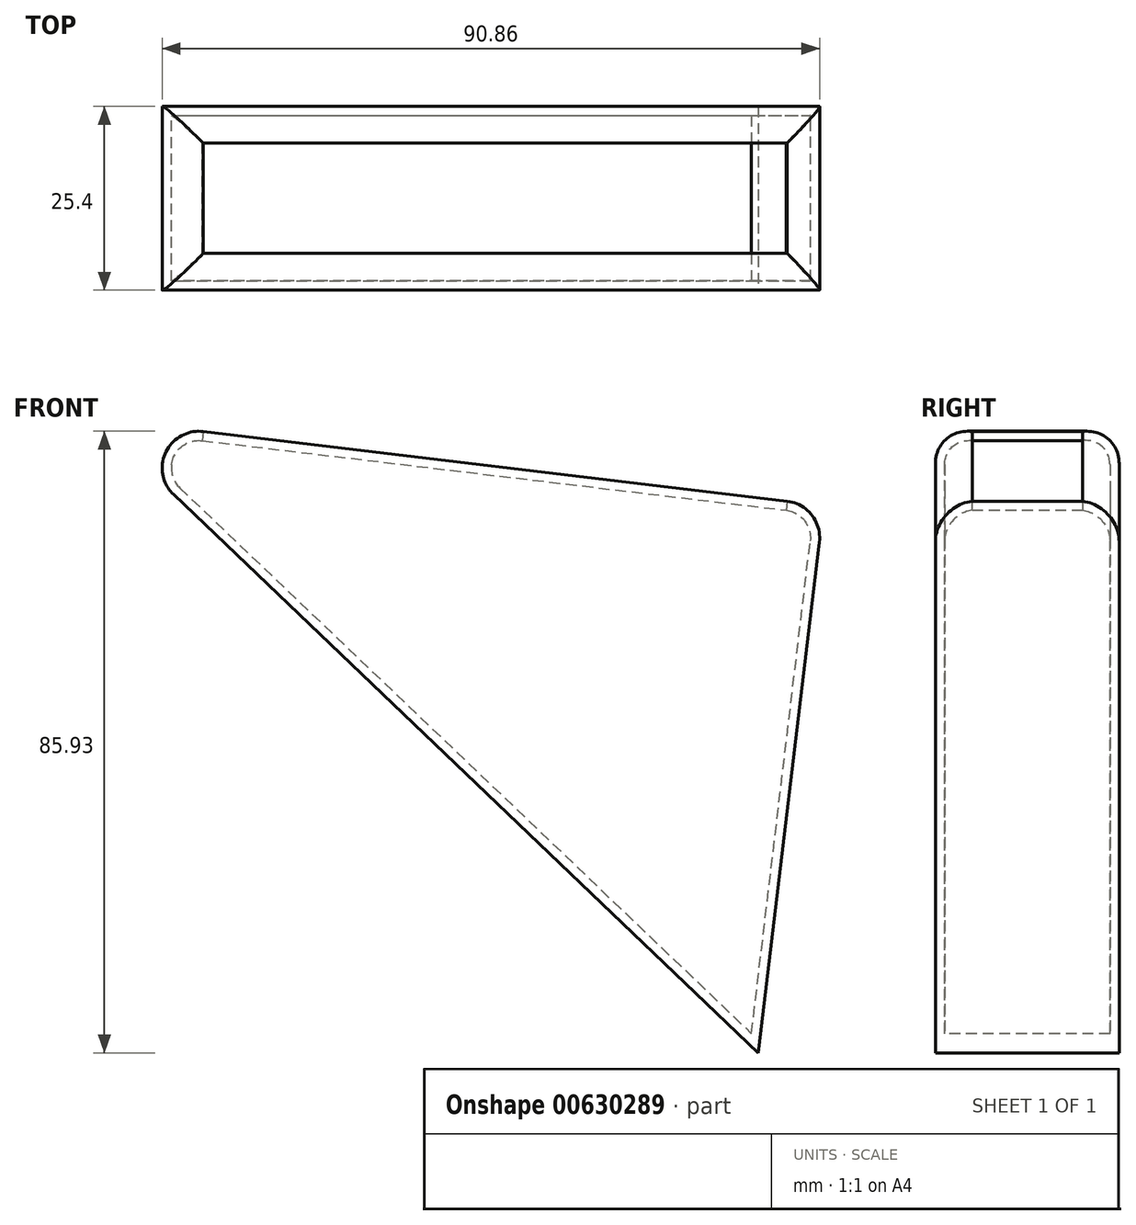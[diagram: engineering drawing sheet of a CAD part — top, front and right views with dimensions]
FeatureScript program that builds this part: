
annotation { "Feature Type Name" : "Feature", "Feature Type Description" : "" }
export const myFeature = defineFeature(function(context is Context, id is Id, definition is map)
    precondition{}
    {
        {
            var Q0;
            Q0=qCreatedBy(makeId("Front.planeOp"),FACE);
            var sketch = newSketch(context, id + "F0", { "sketchPlane" : qUnion([Q0])});
            skLineSegment(sketch, "E0", {"start": v(-110.78, 87.7) * mm, "end": v(-18.92, 0) * mm});
            skLineSegment(sketch, "E1", {"start": v(-18.92, 0) * mm, "end": v(-9.9, 75.66) * mm});
            skLineSegment(sketch, "E2", {"start": v(-110.78, 87.7) * mm, "end": v(-9.9, 75.66) * mm});
            skSolve(sketch);
        }
        {
            var Q0;
            Q0=makeQuery(id+"F0.imprint","IMPRINT",FACE,{"disambiguationData":[TD([[makeQuery(id+"F0.imprint","IMPRINT",EDGE,{"derivedFrom":sQuery(id+"F0.wireOp",EDGE,"E0")}),1.0]])]});
            extrude(context, id + "F1", {"entities" : qUnion([Q0]), "oppositeDirection" : true, "depth" : 25.4 * mm, "offsetDistance" : 25.4 * mm});
        }
        {
            var Q0;
            Q0=makeQuery(id+"F1.opExtrude","CAP_EDGE",EDGE,{"disambiguationData":[OSD([sQuery(id+"F0.wireOp",EDGE,"E2")])],"isStart":true});
            var Q1;
            Q1=makeQuery(id+"F1.opExtrude","SWEPT_EDGE",EDGE,{"disambiguationData":[OSD([sQuery(id+"F0.wireOp",EDGE,"E0"),sQuery(id+"F0.wireOp",EDGE,"E2")])]});
            var Q2;
            Q2=makeQuery(id+"F1.opExtrude","CAP_EDGE",EDGE,{"disambiguationData":[OSD([sQuery(id+"F0.wireOp",EDGE,"E2")])],"isStart":false});
            var Q3;
            Q3=makeQuery(id+"F1.opExtrude","SWEPT_EDGE",EDGE,{"disambiguationData":[OSD([sQuery(id+"F0.wireOp",EDGE,"E1"),sQuery(id+"F0.wireOp",EDGE,"E2")])]});
            fillet(context, id + "F2", {"entities" : qUnion([Q0, Q1, Q2, Q3]), "radius" : 5.08 * mm, "tangentPropagation" : true, "allowEdgeOverflow" : false});
        }
        {
            var Q0;
            Q0=makeQuery(id+"F1.opExtrude","SWEPT_FACE",FACE,{"disambiguationData":[OSD([sQuery(id+"F0.wireOp",EDGE,"E2")])]});
            shell(context, id + "F3", {"entities" : qUnion([Q0]), "thickness" : 1.27 * mm});
        }
    });
